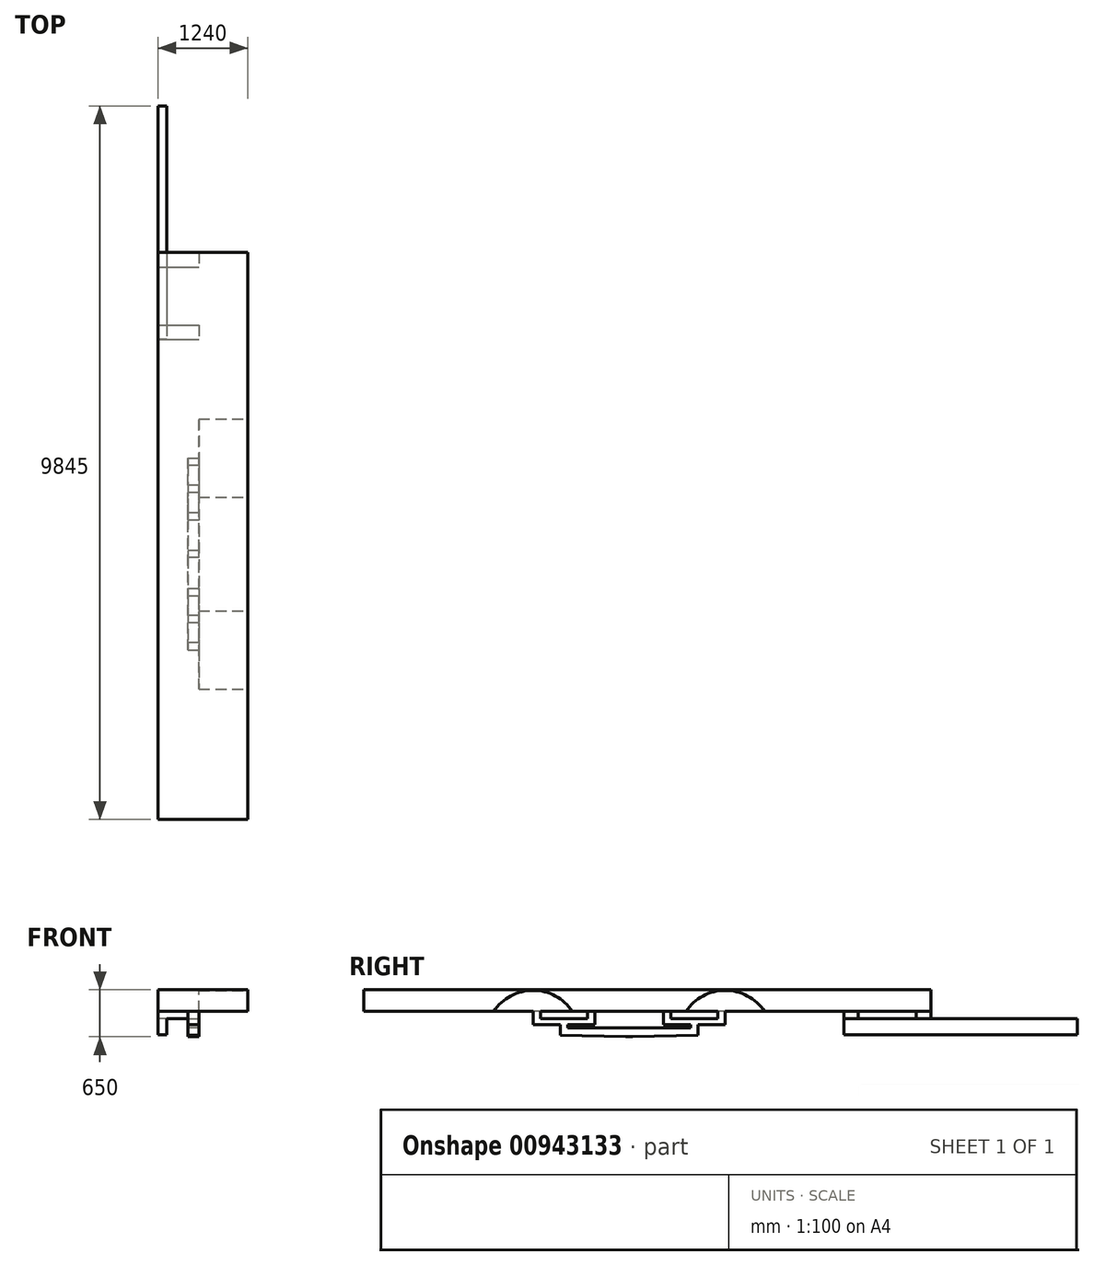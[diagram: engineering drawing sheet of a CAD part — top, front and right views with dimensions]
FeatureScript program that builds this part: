
annotation { "Feature Type Name" : "Feature", "Feature Type Description" : "" }
export const myFeature = defineFeature(function(context is Context, id is Id, definition is map)
    precondition{}
    {
        {
            var Q0;
            Q0=qCreatedBy(makeId("Top.planeOp"),FACE);
            var sketch = newSketch(context, id + "F0", { "sketchPlane" : qUnion([Q0])});
            skLineSegment(sketch, "E0.bottom", {"start": v(1240, 3910) * mm, "end": v(-1240, 3910) * mm});
            skLineSegment(sketch, "E0.top", {"start": v(1240, -3910) * mm, "end": v(-1240, -3910) * mm});
            skLineSegment(sketch, "E0.left", {"start": v(1240, 3910) * mm, "end": v(1240, -3910) * mm});
            skLineSegment(sketch, "E0.right", {"start": v(-1240, 3910) * mm, "end": v(-1240, -3910) * mm});
            skLineSegment(sketch, "E1", {"start": v(1240, 0) * mm, "end": v(-1240, 0) * mm, "construction": true});
            skSolve(sketch);
        }
        {
            var Q0;
            Q0=makeQuery(id+"F0.imprint","IMPRINT",FACE,{"disambiguationData":[TD([[makeQuery(id+"F0.imprint","IMPRINT",EDGE,{"derivedFrom":sQuery(id+"F0.wireOp",EDGE,"E0.bottom")}),1.0]])]});
            extrude(context, id + "F1", {"entities" : qUnion([Q0]), "depth" : 300 * mm, "offsetDistance" : 25 * mm});
        }
        {
            var Q0;
            Q0=makeQuery(id+"F1.opExtrude","CAP_FACE",FACE,{"disambiguationData":[OSD([sQuery(id+"F0.wireOp",EDGE,"E0.bottom"),sQuery(id+"F0.wireOp",EDGE,"E0.top"),sQuery(id+"F0.wireOp",EDGE,"E0.left"),sQuery(id+"F0.wireOp",EDGE,"E0.right")])],"isStart":true});
            var sketch = newSketch(context, id + "F2", { "sketchPlane" : qUnion([Q0])});
            skLineSegment(sketch, "E2.bottom", {"start": v(-565, -3910) * mm, "end": v(565, -3910) * mm});
            skLineSegment(sketch, "E2.top", {"start": v(-565, -3710) * mm, "end": v(565, -3710) * mm});
            skLineSegment(sketch, "E2.left", {"start": v(-565, -3910) * mm, "end": v(-565, -3710) * mm});
            skLineSegment(sketch, "E2.right", {"start": v(565, -3910) * mm, "end": v(565, -3710) * mm});
            skLineSegment(sketch, "E3.bottom", {"start": v(-565, -2910) * mm, "end": v(565, -2910) * mm});
            skLineSegment(sketch, "E3.top", {"start": v(-565, -2710) * mm, "end": v(565, -2710) * mm});
            skLineSegment(sketch, "E3.left", {"start": v(-565, -2910) * mm, "end": v(-565, -2710) * mm});
            skLineSegment(sketch, "E3.right", {"start": v(565, -2910) * mm, "end": v(565, -2710) * mm});
            skLineSegment(sketch, "E4", {"start": v(0, 0) * mm, "end": v(0, -3910) * mm, "construction": true});
            skLineSegment(sketch, "E5.bottom", {"start": v(-565, -1075) * mm, "end": v(-415, -1075) * mm});
            skLineSegment(sketch, "E5.top", {"start": v(-565, 1575) * mm, "end": v(-415, 1575) * mm});
            skLineSegment(sketch, "E5.left", {"start": v(-565, -1075) * mm, "end": v(-565, 1575) * mm});
            skLineSegment(sketch, "E5.right", {"start": v(-415, -1075) * mm, "end": v(-415, 1575) * mm});
            skLineSegment(sketch, "E6.bottom", {"start": v(415, -1075) * mm, "end": v(565, -1075) * mm});
            skLineSegment(sketch, "E6.top", {"start": v(415, 1575) * mm, "end": v(565, 1575) * mm});
            skLineSegment(sketch, "E6.left", {"start": v(415, -1075) * mm, "end": v(415, 1575) * mm});
            skLineSegment(sketch, "E6.right", {"start": v(565, -1075) * mm, "end": v(565, 1575) * mm});
            skLineSegment(sketch, "E7", {"start": v(-490, 1575) * mm, "end": v(-490, -1075) * mm, "construction": true});
            skLineSegment(sketch, "E8", {"start": v(490, -1075) * mm, "end": v(490, 1575) * mm, "construction": true});
            skLineSegment(sketch, "E9", {"start": v(565, 1475) * mm, "end": v(415, 1475) * mm});
            skLineSegment(sketch, "E10", {"start": v(565, -975) * mm, "end": v(415, -975) * mm});
            skLineSegment(sketch, "E11", {"start": v(-415, 1475) * mm, "end": v(-565, 1475) * mm});
            skLineSegment(sketch, "E12", {"start": v(-415, -975) * mm, "end": v(-565, -975) * mm});
            skLineSegment(sketch, "E13.bottom", {"start": v(-565, -325) * mm, "end": v(-415, -325) * mm});
            skLineSegment(sketch, "E13.top", {"start": v(-565, -225) * mm, "end": v(-415, -225) * mm});
            skLineSegment(sketch, "E13.left", {"start": v(-565, -325) * mm, "end": v(-565, -225) * mm});
            skLineSegment(sketch, "E13.right", {"start": v(-415, -325) * mm, "end": v(-415, -225) * mm});
            skLineSegment(sketch, "E14.bottom", {"start": v(-565, 725) * mm, "end": v(-415, 725) * mm});
            skLineSegment(sketch, "E14.top", {"start": v(-565, 825) * mm, "end": v(-415, 825) * mm});
            skLineSegment(sketch, "E14.left", {"start": v(-565, 725) * mm, "end": v(-565, 825) * mm});
            skLineSegment(sketch, "E14.right", {"start": v(-415, 725) * mm, "end": v(-415, 825) * mm});
            skLineSegment(sketch, "E15.bottom", {"start": v(415, 725) * mm, "end": v(565, 725) * mm});
            skLineSegment(sketch, "E15.top", {"start": v(415, 825) * mm, "end": v(565, 825) * mm});
            skLineSegment(sketch, "E15.left", {"start": v(415, 725) * mm, "end": v(415, 825) * mm});
            skLineSegment(sketch, "E15.right", {"start": v(565, 725) * mm, "end": v(565, 825) * mm});
            skLineSegment(sketch, "E16.bottom", {"start": v(415, -325) * mm, "end": v(565, -325) * mm});
            skLineSegment(sketch, "E16.top", {"start": v(415, -225) * mm, "end": v(565, -225) * mm});
            skLineSegment(sketch, "E16.left", {"start": v(415, -325) * mm, "end": v(415, -225) * mm});
            skLineSegment(sketch, "E16.right", {"start": v(565, -325) * mm, "end": v(565, -225) * mm});
            skLineSegment(sketch, "E17", {"start": v(490, -225) * mm, "end": v(490, -1075) * mm});
            skLineSegment(sketch, "E18", {"start": v(490, -650) * mm, "end": v(-490, -650) * mm, "construction": true});
            skLineSegment(sketch, "E19", {"start": v(490, 725) * mm, "end": v(490, 1575) * mm, "construction": true});
            skLineSegment(sketch, "E20", {"start": v(490, 1150) * mm, "end": v(0, 1150) * mm, "construction": true});
            skLineSegment(sketch, "E21", {"start": v(0, -650) * mm, "end": v(0, 1150) * mm, "construction": true});
            skPoint(sketch, "E22", {"position": v(0, 250) * mm});
            skSolve(sketch);
        }
        {
            var Q0;
            Q0=makeQuery(id+"F2.imprint","IMPRINT",FACE,{"disambiguationData":[TD([[makeQuery(id+"F2.imprint","IMPRINT",EDGE,{"derivedFrom":sQuery(id+"F2.wireOp",EDGE,"E3.bottom")}),1.0]])]});
            var Q1;
            Q1=makeQuery(id+"F2.imprint","IMPRINT",FACE,{"disambiguationData":[TD([[makeQuery(id+"F2.imprint","IMPRINT",EDGE,{"derivedFrom":sQuery(id+"F2.wireOp",EDGE,"E2.bottom")}),-1.0]])]});
            var Q2;
            {var subQ0=sQuery(id+"F2.wireOp",EDGE,"E5.bottom");Q2=makeQuery(id+"F2.imprint","IMPRINT",FACE,{"disambiguationData":[TD([[makeQuery(id+"F2.imprint","IMPRINT",EDGE,{"derivedFrom":subQ0}),1.0]])]});}
            var Q3;
            {var subQ0=sQuery(id+"F2.wireOp",EDGE,"E6.right");var subQ1=sQuery(id+"F2.wireOp",EDGE,"E6.bottom");var subQ2=makeQuery(id+"F2.imprint","INTERSECT",VERTEX,{"derivedFrom":[subQ1,subQ0]});var subQ9=sQuery(id+"F2.wireOp",EDGE,"E6.left");var subQ10=makeQuery(id+"F2.imprint","INTERSECT",VERTEX,{"derivedFrom":[subQ1,subQ9]});Q3=qUnion([makeQuery(id+"F2.imprint","IMPRINT",FACE,{"disambiguationData":[TD([[makeQuery(id+"F2.imprint","IMPRINT",EDGE,{"disambiguationData":[TD([[subQ10,-1.0]])],"derivedFrom":subQ1}),1.0]])]}),makeQuery(id+"F2.imprint","IMPRINT",FACE,{"disambiguationData":[TD([[makeQuery(id+"F2.imprint","IMPRINT",EDGE,{"disambiguationData":[TD([[subQ2,1.0]])],"derivedFrom":subQ1}),1.0]])]})]);}
            var Q4;
            {var subQ0=sQuery(id+"F2.wireOp",EDGE,"E6.top");Q4=makeQuery(id+"F2.imprint","IMPRINT",FACE,{"disambiguationData":[TD([[makeQuery(id+"F2.imprint","IMPRINT",EDGE,{"derivedFrom":subQ0}),-1.0]])]});}
            var Q5;
            {var subQ0=sQuery(id+"F2.wireOp",EDGE,"E5.top");Q5=makeQuery(id+"F2.imprint","IMPRINT",FACE,{"disambiguationData":[TD([[makeQuery(id+"F2.imprint","IMPRINT",EDGE,{"derivedFrom":subQ0}),-1.0]])]});}
            var Q6;
            {var subQ2=sQuery(id+"F2.wireOp",EDGE,"E13.bottom");Q6=makeQuery(id+"F2.imprint","IMPRINT",FACE,{"disambiguationData":[TD([[makeQuery(id+"F2.imprint","IMPRINT",EDGE,{"derivedFrom":subQ2}),1.0]])]});}
            var Q7;
            {var subQ0=sQuery(id+"F2.wireOp",EDGE,"E16.top");var subQ1=sQuery(id+"F2.wireOp",EDGE,"E6.left");var subQ2=makeQuery(id+"F2.imprint","INTERSECT",VERTEX,{"derivedFrom":[subQ1,subQ0]});Q7=makeQuery(id+"F2.imprint","IMPRINT",FACE,{"disambiguationData":[TD([[makeQuery(id+"F2.imprint","IMPRINT",EDGE,{"disambiguationData":[TD([[subQ2,1.0]])],"derivedFrom":subQ1}),-1.0]])]});}
            var Q8;
            {var subQ0=sQuery(id+"F2.wireOp",EDGE,"E16.top");var subQ1=sQuery(id+"F2.wireOp",EDGE,"E6.right");var subQ2=makeQuery(id+"F2.imprint","INTERSECT",VERTEX,{"derivedFrom":[subQ1,subQ0]});Q8=makeQuery(id+"F2.imprint","IMPRINT",FACE,{"disambiguationData":[TD([[makeQuery(id+"F2.imprint","IMPRINT",EDGE,{"disambiguationData":[TD([[subQ2,1.0]])],"derivedFrom":subQ1}),1.0]])]});}
            var Q9;
            {var subQ0=sQuery(id+"F2.wireOp",EDGE,"E15.bottom");Q9=makeQuery(id+"F2.imprint","IMPRINT",FACE,{"disambiguationData":[TD([[makeQuery(id+"F2.imprint","IMPRINT",EDGE,{"derivedFrom":subQ0}),1.0]])]});}
            var Q10;
            {var subQ2=sQuery(id+"F2.wireOp",EDGE,"E14.bottom");Q10=makeQuery(id+"F2.imprint","IMPRINT",FACE,{"disambiguationData":[TD([[makeQuery(id+"F2.imprint","IMPRINT",EDGE,{"derivedFrom":subQ2}),1.0]])]});}
            extrude(context, id + "F3", {"entities" : qUnion([Q0, Q1, Q2, Q3, Q4, Q5, Q6, Q7, Q8, Q9, Q10]), "operationType" : NewBodyOperationType.ADD, "depth" : 100 * mm, "offsetDistance" : 25 * mm});
        }
        {
            var Q0;
            Q0=makeQuery(id+"F3.opExtrude","SWEPT_FACE",FACE,{"disambiguationData":[OSD([sQuery(id+"F2.wireOp",EDGE,"E3.top")])]});
            var sketch = newSketch(context, id + "F4", { "sketchPlane" : qUnion([Q0])});
            skLineSegment(sketch, "E23", {"start": v(0, -100) * mm, "end": v(0, -320) * mm, "construction": true});
            skLineSegment(sketch, "E24.bottom", {"start": v(120, -100) * mm, "end": v(-120, -100) * mm});
            skLineSegment(sketch, "E24.top", {"start": v(120, -320) * mm, "end": v(-120, -320) * mm});
            skLineSegment(sketch, "E24.left", {"start": v(120, -100) * mm, "end": v(120, -320) * mm});
            skLineSegment(sketch, "E24.right", {"start": v(-120, -100) * mm, "end": v(-120, -320) * mm});
            skSolve(sketch);
        }
        {
            var Q0;
            Q0=makeQuery(id+"F4.imprint","IMPRINT",FACE,{"disambiguationData":[TD([[makeQuery(id+"F4.imprint","IMPRINT",EDGE,{"derivedFrom":sQuery(id+"F4.wireOp",EDGE,"E24.bottom")}),-1.0]])]});
            extrude(context, id + "F5", {"entities" : qUnion([Q0]), "operationType" : NewBodyOperationType.ADD, "oppositeDirection" : true, "depth" : (1000 + 2225) * mm, "offsetDistance" : 25 * mm});
        }
        {
            var Q0;
            Q0=makeQuery(id+"F1.opExtrude","SWEPT_FACE",FACE,{"disambiguationData":[OSD([sQuery(id+"F0.wireOp",EDGE,"E0.left")])]});
            var sketch = newSketch(context, id + "F6", { "sketchPlane" : qUnion([Q0])});
            skLineSegment(sketch, "E25", {"start": v(-1575, 0) * mm, "end": v(-1575, -360) * mm, "construction": true});
            skLineSegment(sketch, "E26", {"start": v(1075, 0) * mm, "end": v(1075, -360) * mm, "construction": true});
            skCircle(sketch, "E27", {"center": v(-1575, -360) * mm, "radius": 650 * mm});
            skCircle(sketch, "E28", {"center": v(1075, -360) * mm, "radius": 650 * mm});
            skSolve(sketch);
        }
        {
            var Q0;
            Q0 = qSketchRegion(id + "F6", true);
            var Q1;
            {var subQ0=sQuery(id+"F2.wireOp",EDGE,"E6.right");Q1=makeQuery(id+"F3.opExtrude","SWEPT_FACE",FACE,{"disambiguationData":[OSD([subQ0]),TDD([makeQuery(id+"F2.imprint","IMPRINT",EDGE,{"disambiguationData":[TD([[makeQuery(id+"F2.imprint","INTERSECT",VERTEX,{"derivedFrom":[sQuery(id+"F2.wireOp",EDGE,"E6.top"),subQ0]}),1.0]])],"derivedFrom":subQ0})])]});}
            extrude(context, id + "F7", {"entities" : qUnion([Q0]), "operationType" : NewBodyOperationType.REMOVE, "endBound" : BoundingType.UP_TO_SURFACE, "oppositeDirection" : true, "depth" : 850 * mm, "endBoundEntityFace" : qUnion([Q1]), "offsetDistance" : 25 * mm});
        }
        {
            var Q0;
            Q0=makeQuery(id+"F1.opExtrude","CAP_FACE",FACE,{"disambiguationData":[OSD([sQuery(id+"F0.wireOp",EDGE,"E0.bottom"),sQuery(id+"F0.wireOp",EDGE,"E0.top"),sQuery(id+"F0.wireOp",EDGE,"E0.left"),sQuery(id+"F0.wireOp",EDGE,"E0.right")])],"isStart":false});
            var sketch = newSketch(context, id + "F8", { "sketchPlane" : qUnion([Q0])});
            skLineSegment(sketch, "E29.bottom", {"start": v(0, 5935) * mm, "end": v(-1240, 5935) * mm});
            skLineSegment(sketch, "E29.top", {"start": v(0, -3910) * mm, "end": v(-1240, -3910) * mm});
            skLineSegment(sketch, "E29.left", {"start": v(0, 5935) * mm, "end": v(0, -3910) * mm});
            skLineSegment(sketch, "E29.right", {"start": v(-1240, 5935) * mm, "end": v(-1240, -3910) * mm});
            skSolve(sketch);
        }
        {
            var Q0;
            {var subQ0=sQuery(id+"F8.wireOp",EDGE,"E29.bottom");Q0=makeQuery(id+"F8.imprint","IMPRINT",FACE,{"disambiguationData":[TD([[makeQuery(id+"F8.imprint","IMPRINT",EDGE,{"derivedFrom":subQ0}),1.0]])]});}
            var Q1;
            {var subQ0=sQuery(id+"F8.wireOp",EDGE,"E29.top");Q1=makeQuery(id+"F8.imprint","IMPRINT",FACE,{"disambiguationData":[TD([[makeQuery(id+"F8.imprint","IMPRINT",EDGE,{"derivedFrom":subQ0}),-1.0]])]});}
            extrude(context, id + "F9", {"entities" : qUnion([Q0, Q1]), "operationType" : NewBodyOperationType.REMOVE, "oppositeDirection" : true, "depth" : 1420 * mm, "offsetDistance" : 25 * mm});
        }
        {
            var Q0;
            {var subQ0=sQuery(id+"F2.wireOp",EDGE,"E6.left");Q0=makeQuery(id+"F3.opExtrude","SWEPT_FACE",FACE,{"disambiguationData":[OSD([subQ0]),TDD([makeQuery(id+"F2.imprint","IMPRINT",EDGE,{"disambiguationData":[TD([[makeQuery(id+"F2.imprint","INTERSECT",VERTEX,{"derivedFrom":[sQuery(id+"F2.wireOp",EDGE,"E6.bottom"),subQ0]}),-1.0]])],"derivedFrom":subQ0})])]});}
            var sketch = newSketch(context, id + "F10", { "sketchPlane" : qUnion([Q0])});
            skLineSegment(sketch, "E30", {"start": v(725, -100) * mm, "end": v(1575, -100) * mm});
            skLineSegment(sketch, "E31", {"start": v(-1075, -100) * mm, "end": v(-225, -100) * mm});
            skLineSegment(sketch, "E32", {"start": v(1575, -100) * mm, "end": v(1575, -180) * mm});
            skLineSegment(sketch, "E33", {"start": v(1575, -180) * mm, "end": v(725, -180) * mm});
            skLineSegment(sketch, "E34", {"start": v(725, -180) * mm, "end": v(725, -100) * mm});
            skLineSegment(sketch, "E35", {"start": v(-225, -100) * mm, "end": v(-225, -180) * mm});
            skLineSegment(sketch, "E36", {"start": v(-225, -180) * mm, "end": v(-1075, -180) * mm});
            skLineSegment(sketch, "E37", {"start": v(-1075, -180) * mm, "end": v(-1075, -100) * mm});
            skLineSegment(sketch, "E38", {"start": v(1150, -180) * mm, "end": v(1150, -300.24) * mm, "construction": true});
            skLineSegment(sketch, "E39", {"start": v(-650, -180) * mm, "end": v(-650, -290.37) * mm, "construction": true});
            skLineSegment(sketch, "E40", {"start": v(1100, -180) * mm, "end": v(1100, -230) * mm});
            skLineSegment(sketch, "E41", {"start": v(1100, -230) * mm, "end": v(-600, -230) * mm});
            skLineSegment(sketch, "E42", {"start": v(-600, -230) * mm, "end": v(-600, -180) * mm});
            skLineSegment(sketch, "E43", {"start": v(-600, -180) * mm, "end": v(-700, -180) * mm});
            skLineSegment(sketch, "E44", {"start": v(-700, -180) * mm, "end": v(-700, -330) * mm});
            skLineSegment(sketch, "E45", {"start": v(-700, -330) * mm, "end": v(200, -350) * mm});
            skLineSegment(sketch, "E46", {"start": v(200, -350) * mm, "end": v(300, -350) * mm});
            skLineSegment(sketch, "E47", {"start": v(300, -350) * mm, "end": v(1200, -330) * mm});
            skLineSegment(sketch, "E48", {"start": v(1200, -330) * mm, "end": v(1200, -180) * mm});
            skSolve(sketch);
        }
        {
            var Q0;
            {var subQ0=sQuery(id+"F10.wireOp",EDGE,"E40");var subQ13=sQuery(id+"F10.wireOp",EDGE,"E35");Q0=qUnion([makeQuery(id+"F10.imprint","IMPRINT",FACE,{"disambiguationData":[TD([[makeQuery(id+"F10.imprint","IMPRINT",EDGE,{"derivedFrom":sQuery(id+"F10.wireOp",EDGE,"E30")}),-1.0]])]}),makeQuery(id+"F10.imprint","IMPRINT",FACE,{"disambiguationData":[TD([[makeQuery(id+"F10.imprint","IMPRINT",EDGE,{"derivedFrom":subQ13}),-1.0]])]}),makeQuery(id+"F10.imprint","IMPRINT",FACE,{"disambiguationData":[TD([[makeQuery(id+"F10.imprint","IMPRINT",EDGE,{"derivedFrom":subQ0}),1.0]])]})]);}
            var Q1;
            {var subQ0=sQuery(id+"F2.wireOp",EDGE,"E6.right");Q1=makeQuery(id+"F7.boolean.opBoolean","MERGE",FACE,{"derivedFrom":[makeQuery(id+"F3.opExtrude","SWEPT_FACE",FACE,{"disambiguationData":[OSD([subQ0]),TDD([makeQuery(id+"F2.imprint","IMPRINT",EDGE,{"disambiguationData":[TD([[makeQuery(id+"F2.imprint","INTERSECT",VERTEX,{"derivedFrom":[sQuery(id+"F2.wireOp",EDGE,"E6.top"),subQ0]}),1.0]])],"derivedFrom":subQ0})])]})],"fromTools":[makeQuery(id+"F7.opExtrude","CAP_FACE",FACE,{"disambiguationData":[OSD([sQuery(id+"F6.wireOp",EDGE,"E27")])],"isStart":false})]});}
            extrude(context, id + "F11", {"entities" : qUnion([Q0]), "operationType" : NewBodyOperationType.ADD, "endBound" : BoundingType.UP_TO_SURFACE, "oppositeDirection" : true, "depth" : 25 * mm, "endBoundEntityFace" : qUnion([Q1]), "offsetDistance" : 25 * mm});
        }
    });
